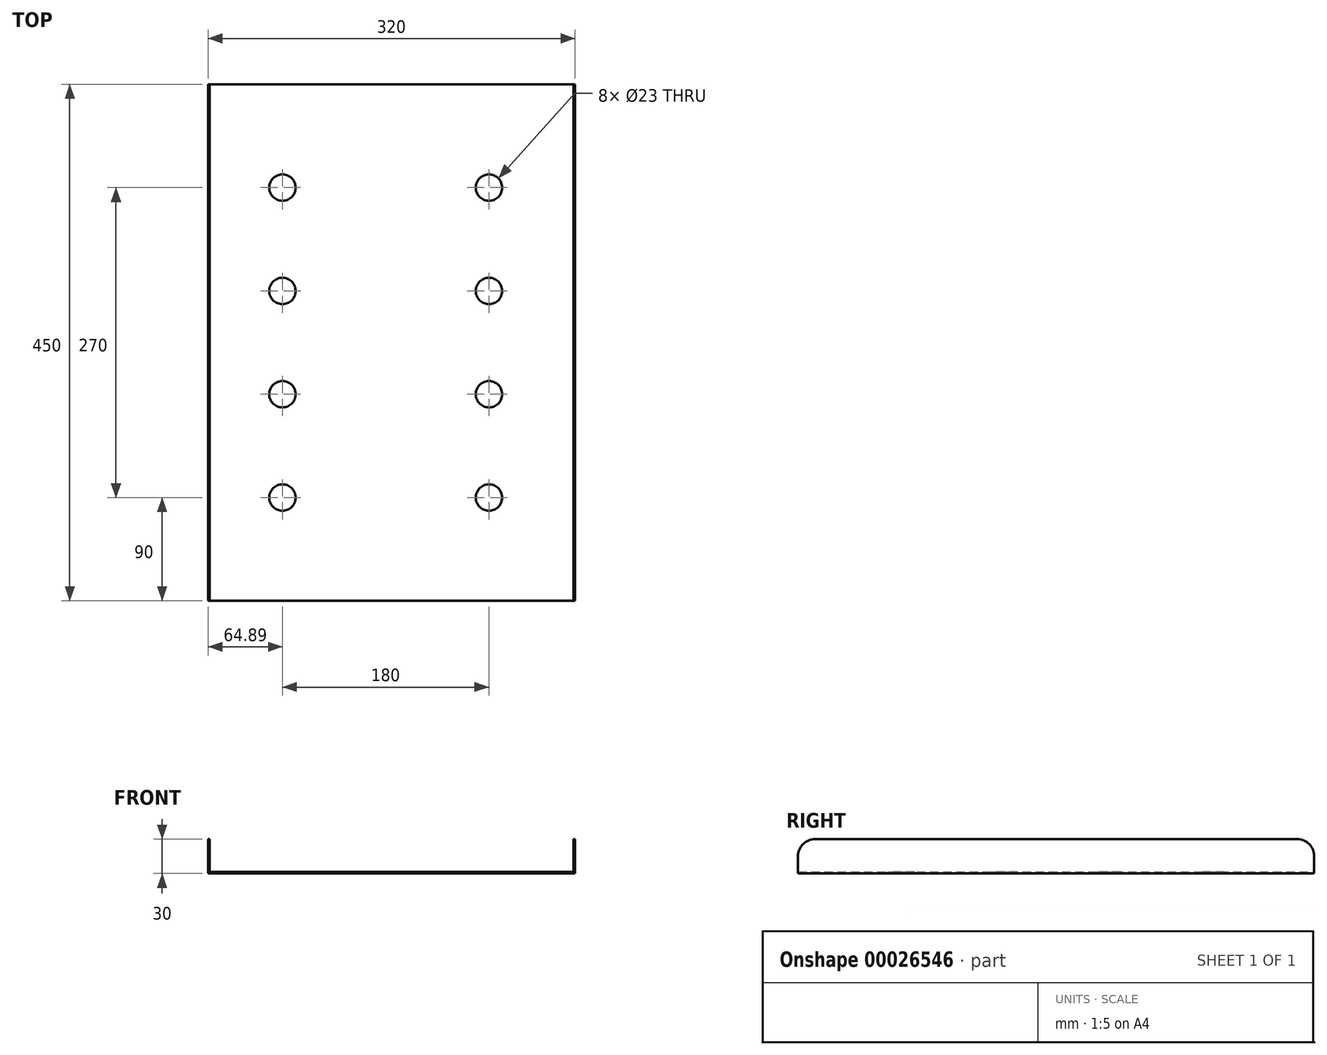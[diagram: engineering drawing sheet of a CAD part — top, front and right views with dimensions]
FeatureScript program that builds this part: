
annotation { "Feature Type Name" : "Feature", "Feature Type Description" : "" }
export const myFeature = defineFeature(function(context is Context, id is Id, definition is map)
    precondition{}
    {
        {
            var Q0;
            Q0=qCreatedBy(makeId("Front.planeOp"),FACE);
            var sketch = newSketch(context, id + "F0", { "sketchPlane" : qUnion([Q0])});
            skLineSegment(sketch, "E0", {"start": v(-154.9, -23.54) * mm, "end": v(-154.9, -53.54) * mm});
            skLineSegment(sketch, "E1", {"start": v(-154.9, -53.54) * mm, "end": v(165.1, -53.54) * mm});
            skLineSegment(sketch, "E2", {"start": v(165.1, -53.54) * mm, "end": v(165.1, -23.54) * mm});
            skLineSegment(sketch, "E3.0", {"start": v(-153.4, -23.54) * mm, "end": v(-153.4, -52.04) * mm});
            skLineSegment(sketch, "E4.0", {"start": v(-153.4, -52.04) * mm, "end": v(163.6, -52.04) * mm});
            skLineSegment(sketch, "E5.0", {"start": v(163.6, -52.04) * mm, "end": v(163.6, -23.54) * mm});
            skLineSegment(sketch, "E6", {"start": v(-154.9, -23.54) * mm, "end": v(-153.4, -23.54) * mm});
            skLineSegment(sketch, "E7", {"start": v(163.6, -23.54) * mm, "end": v(165.1, -23.54) * mm});
            skSolve(sketch);
        }
        {
            var Q0;
            Q0=makeQuery(id+"F0.imprint","IMPRINT",FACE,{"disambiguationData":[TD([[makeQuery(id+"F0.imprint","IMPRINT",EDGE,{"derivedFrom":sQuery(id+"F0.wireOp",EDGE,"E0")}),1.0]])]});
            extrude(context, id + "F1", {"entities" : qUnion([Q0]), "depth" : 450 * mm});
        }
        {
            var Q0;
            Q0=makeQuery(id+"F1.opExtrude","CAP_EDGE",EDGE,{"disambiguationData":[OSD([sQuery(id+"F0.wireOp",EDGE,"E6")])],"isStart":true});
            var Q1;
            Q1=makeQuery(id+"F1.opExtrude","CAP_EDGE",EDGE,{"disambiguationData":[OSD([sQuery(id+"F0.wireOp",EDGE,"E7")])],"isStart":true});
            var Q2;
            Q2=makeQuery(id+"F1.opExtrude","CAP_EDGE",EDGE,{"disambiguationData":[OSD([sQuery(id+"F0.wireOp",EDGE,"E7")])],"isStart":false});
            var Q3;
            Q3=makeQuery(id+"F1.opExtrude","CAP_EDGE",EDGE,{"disambiguationData":[OSD([sQuery(id+"F0.wireOp",EDGE,"E6")])],"isStart":false});
            fillet(context, id + "F2", {"entities" : qUnion([Q0, Q1, Q2, Q3]), "radius" : 15 * mm, "tangentPropagation" : true, "allowEdgeOverflow" : false});
        }
        {
            var Q0;
            Q0=makeQuery(id+"F1.opExtrude","SWEPT_FACE",FACE,{"disambiguationData":[OSD([sQuery(id+"F0.wireOp",EDGE,"E4.0")])]});
            var sketch = newSketch(context, id + "F3", { "sketchPlane" : qUnion([Q0])});
            skPoint(sketch, "E8", {"position": v(5.1, -450) * mm});
            skPoint(sketch, "E9", {"position": v(0, 0) * mm});
            skPoint(sketch, "E10", {"position": v(-90, -90) * mm});
            skPoint(sketch, "E11.0.1.0", {"position": v(-90, -180) * mm});
            skPoint(sketch, "E11.0.2.0", {"position": v(-90, -270) * mm});
            skPoint(sketch, "E11.0.3.0", {"position": v(-90, -360) * mm});
            skPoint(sketch, "E11.1.0.0", {"position": v(90, -90) * mm});
            skPoint(sketch, "E11.1.1.0", {"position": v(90, -180) * mm});
            skPoint(sketch, "E11.1.2.0", {"position": v(90, -270) * mm});
            skPoint(sketch, "E11.1.3.0", {"position": v(90, -360) * mm});
            skLineSegment(sketch, "E11.direction1", {"start": v(-90, -90) * mm, "end": v(90, -90) * mm, "construction": true});
            skLineSegment(sketch, "E11.direction2", {"start": v(-90, -90) * mm, "end": v(-90, -180) * mm, "construction": true});
            skSolve(sketch);
        }
        {
            var Q0;
            Q0=sQuery(id+"F3.wireOp",VERTEX,"E10");
            var Q1;
            Q1=sQuery(id+"F3.wireOp",VERTEX,"E11.0.1.0");
            var Q2;
            Q2=sQuery(id+"F3.wireOp",VERTEX,"E11.0.2.0");
            var Q3;
            Q3=sQuery(id+"F3.wireOp",VERTEX,"E11.0.3.0");
            var Q4;
            Q4=sQuery(id+"F3.wireOp",VERTEX,"E11.1.0.0");
            var Q5;
            Q5=sQuery(id+"F3.wireOp",VERTEX,"E11.1.1.0");
            var Q6;
            Q6=sQuery(id+"F3.wireOp",VERTEX,"E11.1.2.0");
            var Q7;
            Q7=sQuery(id+"F3.wireOp",VERTEX,"E11.1.3.0");
            var Q8;
            Q8=makeQuery(id+"F1.opExtrude","SWEPT_BODY",BODY,{"disambiguationData":[OSD([sQuery(id+"F0.wireOp",EDGE,"E0"),sQuery(id+"F0.wireOp",EDGE,"E1"),sQuery(id+"F0.wireOp",EDGE,"E2"),sQuery(id+"F0.wireOp",EDGE,"E3.0"),sQuery(id+"F0.wireOp",EDGE,"E4.0"),sQuery(id+"F0.wireOp",EDGE,"E5.0"),sQuery(id+"F0.wireOp",EDGE,"E6"),sQuery(id+"F0.wireOp",EDGE,"E7")])]});
            hole(context, id + "F4", {"style" : HoleStyle.SIMPLE, "holeDiameter" : 23 * mm, "endStyle" : HoleEndStyle.THROUGH, "locations" : qUnion([Q0, Q1, Q2, Q3, Q4, Q5, Q6, Q7]), "scope" : qUnion([Q8])});
        }
    });
